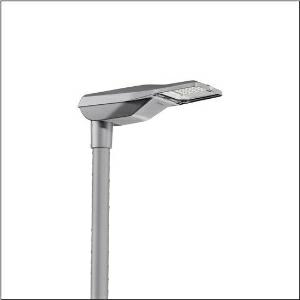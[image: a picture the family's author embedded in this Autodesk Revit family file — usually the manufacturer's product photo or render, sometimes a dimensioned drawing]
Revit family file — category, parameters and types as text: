
# Revit family: streetlight_sl_21_iq_micro___st0_8a_5xe1c61g08cb_671e
name_source: partatom
category: Lighting Fixtures
units: mm (PartAtom-declared; Revit-internal decimal feet)

## family parameters
Cut with Voids When Loaded = No
Host = Face
Light Source = No
Part Type = Normal
Room Calculation Point = No
Round Connector Dimension = Use Diameter
Shared = No

## types (1)
- --- (1 x LED, 2570 lm, 19.4 W, 2700K)
    Apparent Load = 19 VA
    CIE Flux Codes = 38 75 97 100 100
    Color Rendering = 70
    Color Temperature = 2700K
    Default Elevation = 1800 mm
    Description = Streetlight SL 21 iQ micro, mast luminaire, primary light control with lens, of PMMA, primary optical cover: cover, of toughened safety glass, transparent, light distribution: ST0.8a, light emission: direct distribution, primary light characteristic: asymmetric, installation type: post-top, side-entry, LED, High Power LED, rated luminous flux: 2.570lm, luminous efficacy: 133lm/W, light colour: 727, colour temperature: 2700K, control gear: iQ Street-Remote, control: Street-Remote, Auto-Match, Temp-Guard, Lumen-Switch, Night-Set, Smart-Wire, Light-Fading, Desk-Remote (wireless, voltage-free reading and setting of iQ features in the workshop via application-optimized NFC function/RFID function), optimised constant luminous flux control (CLO 2.0), pre-setting: linear dimming characteristic, mains connection: 220..240V, AC, 50/60Hz, start of lifetime: 19W, end of service life: 20W, reduction: 10W, luminaire housing, of diecast aluminium, powder-coated, SITECO metallic grey (DB 702S), corrosivity category C5 high according to DIN EN ISO 12944, please order mast flange separately, inclination adjustable: 0°, 5°, 10°, 15°, sealing non-destructively replaceable, multi-level sealing system, length: 528mm, width: 235mm, height: 110mm, mast flange for spigot size: 42mm (side-entry): 5XC10008XM4, 60/48mm (side-entry/post-top): 5XC10108XM2, 76/60mm (side-entry/post-top): 5XC10108XM1, protection rating (complete): IP66, insulation class (complete): insulation class II (safety insulation), certification: CE, ENEC, ENEC+, VDE, impact resistance: IK10, permissible operating ambient temperature for outdoor applications: -40..+50°C, standard-compliant lighting for roads and squares, packaging unit: 1 piece

Light Distribution: ST0.8a
    Height = 110 mm
    Lamp = 1 x LED
    Lamp Light Flux = 2570 lm
    Lamp Power = 19.4 W
    Lamp count = 1
    Length = 528 mm
    Luminous efficacy = 132 lm/W
    Manufacturer = Siteco
    ModVariant = No
    Model = 5XE1C61G08CB
    Number of Poles = 1
    OnlyDefault = Yes
    Power Factor = 1
    Product Name = Streetlight SL 21 iQ micro | ST0.8a
    Product group = mast luminaire | pylon top
    ProductGroupID = 6100
    Protection Class = Protection class II
    Protection Degree = IP 66
    RLX_Detail_Level = 1
    RLX_Emergency_Light_Flux = 0 lm
    RLX_Emergency_Type = 0
    RLX_Emergency_Type_DB = No
    RlxData = <blob elided: 99241 chars, md5=66bf4c7c>
    Socket = socket
    Standby Power = 0 W
    System Light Flux = 2570 lm
    System Power = 19 W
    Type Comments = factory setting: luminous flux: 100 % | dim-lin: 254 | 387 mA
    Type Image = l_1006881.jpg
    URL = http://relux.com
    VarID = @adj_137779
    Voltage = 0 V
    Weight = 0.00 kg
    Width = 235 mm

## geometry (parser evidence)
native form markers: Blend x4, Sweep x11
no freeform markers — native parametric forms only
